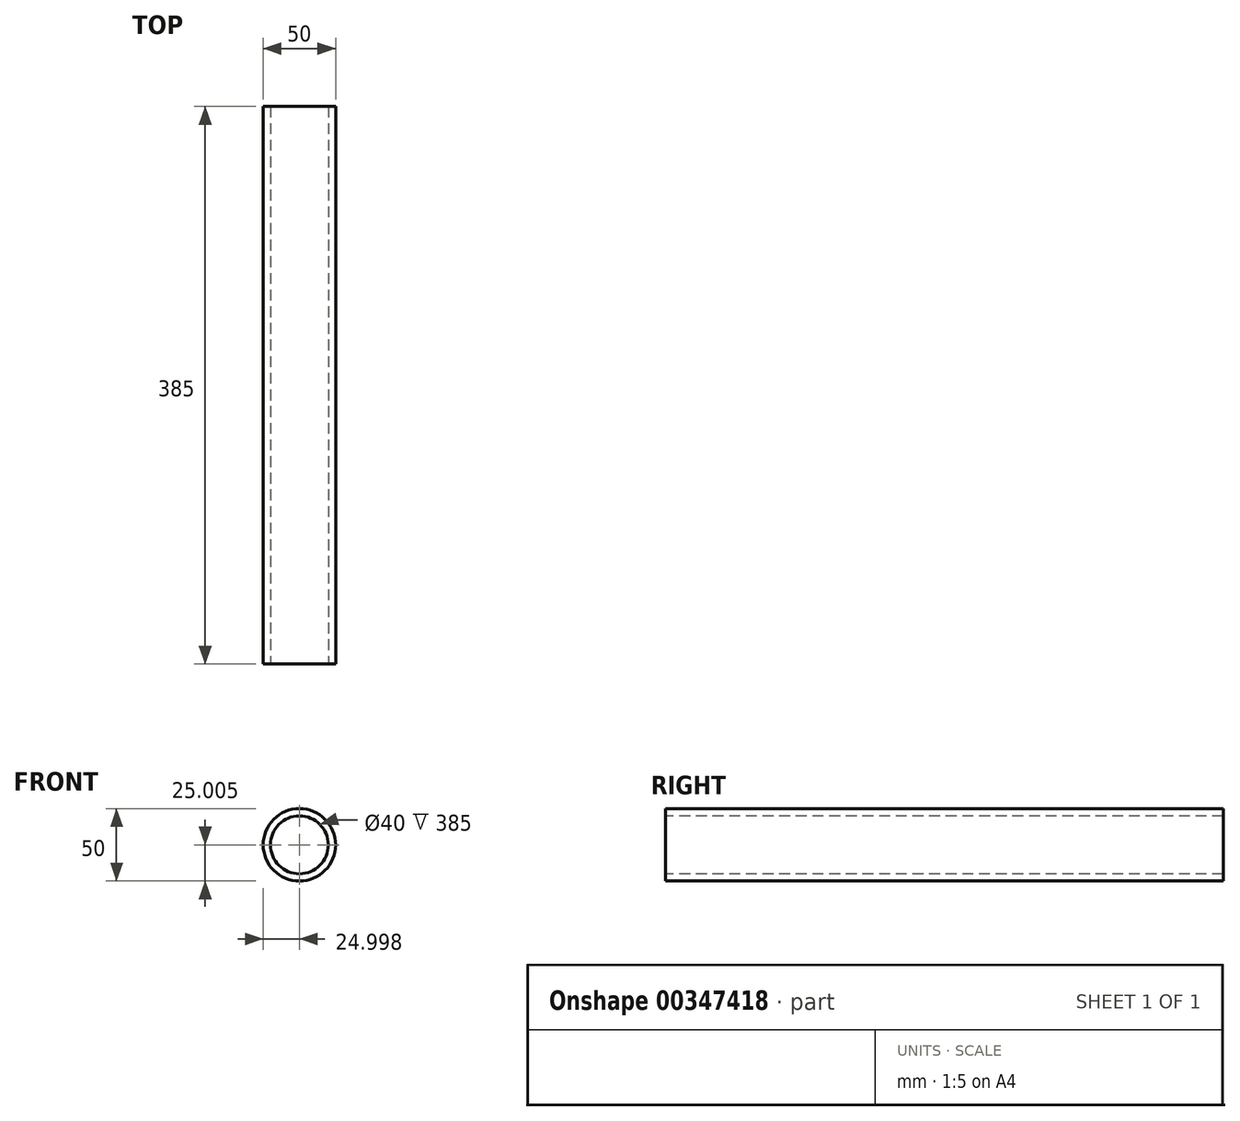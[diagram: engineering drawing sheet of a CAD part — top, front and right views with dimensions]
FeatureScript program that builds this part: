
annotation { "Feature Type Name" : "Feature", "Feature Type Description" : "" }
export const myFeature = defineFeature(function(context is Context, id is Id, definition is map)
    precondition{}
    {
        {
            var Q0;
            Q0=qCreatedBy(makeId("Front.planeOp"),FACE);
            var sketch = newSketch(context, id + "F0", { "sketchPlane" : qUnion([Q0])});
            skCircle(sketch, "E0", {"center": v(-25.11, 20.25) * mm, "radius": 25 * mm});
            skSolve(sketch);
        }
        {
            var Q0;
            Q0=makeQuery(id+"F0.imprint","IMPRINT",FACE,{"disambiguationData":[TD([[makeQuery(id+"F0.imprint","IMPRINT",EDGE,{"derivedFrom":sQuery(id+"F0.wireOp",EDGE,"E0")}),1.0]])]});
            extrude(context, id + "F1", {"entities" : qUnion([Q0]), "depth" : 385 * mm});
        }
        {
            var Q0;
            Q0=makeQuery(id+"F1.opExtrude","CAP_FACE",FACE,{"disambiguationData":[OSD([sQuery(id+"F0.wireOp",EDGE,"E0")])],"isStart":false});
            var sketch = newSketch(context, id + "F2", { "sketchPlane" : qUnion([Q0])});
            skCircle(sketch, "E1", {"center": v(-25.11, 20.25) * mm, "radius": 20 * mm});
            skSolve(sketch);
        }
        {
            var Q0;
            Q0=sQuery(id+"F2.wireOp",VERTEX,"E1.center");
            var Q1;
            Q1=makeQuery(id+"F1.opExtrude","SWEPT_BODY",BODY,{"disambiguationData":[OSD([sQuery(id+"F0.wireOp",EDGE,"E0")])]});
            hole(context, id + "F3", {"style" : HoleStyle.SIMPLE, "endStyle" : HoleEndStyle.THROUGH, "holeDiameter" : 40 * mm, "isTappedThrough" : true, "tappedDepth" : 12 * mm, "tapClearance" : 3, "locations" : qUnion([Q0]), "scope" : qUnion([Q1])});
        }
    });
